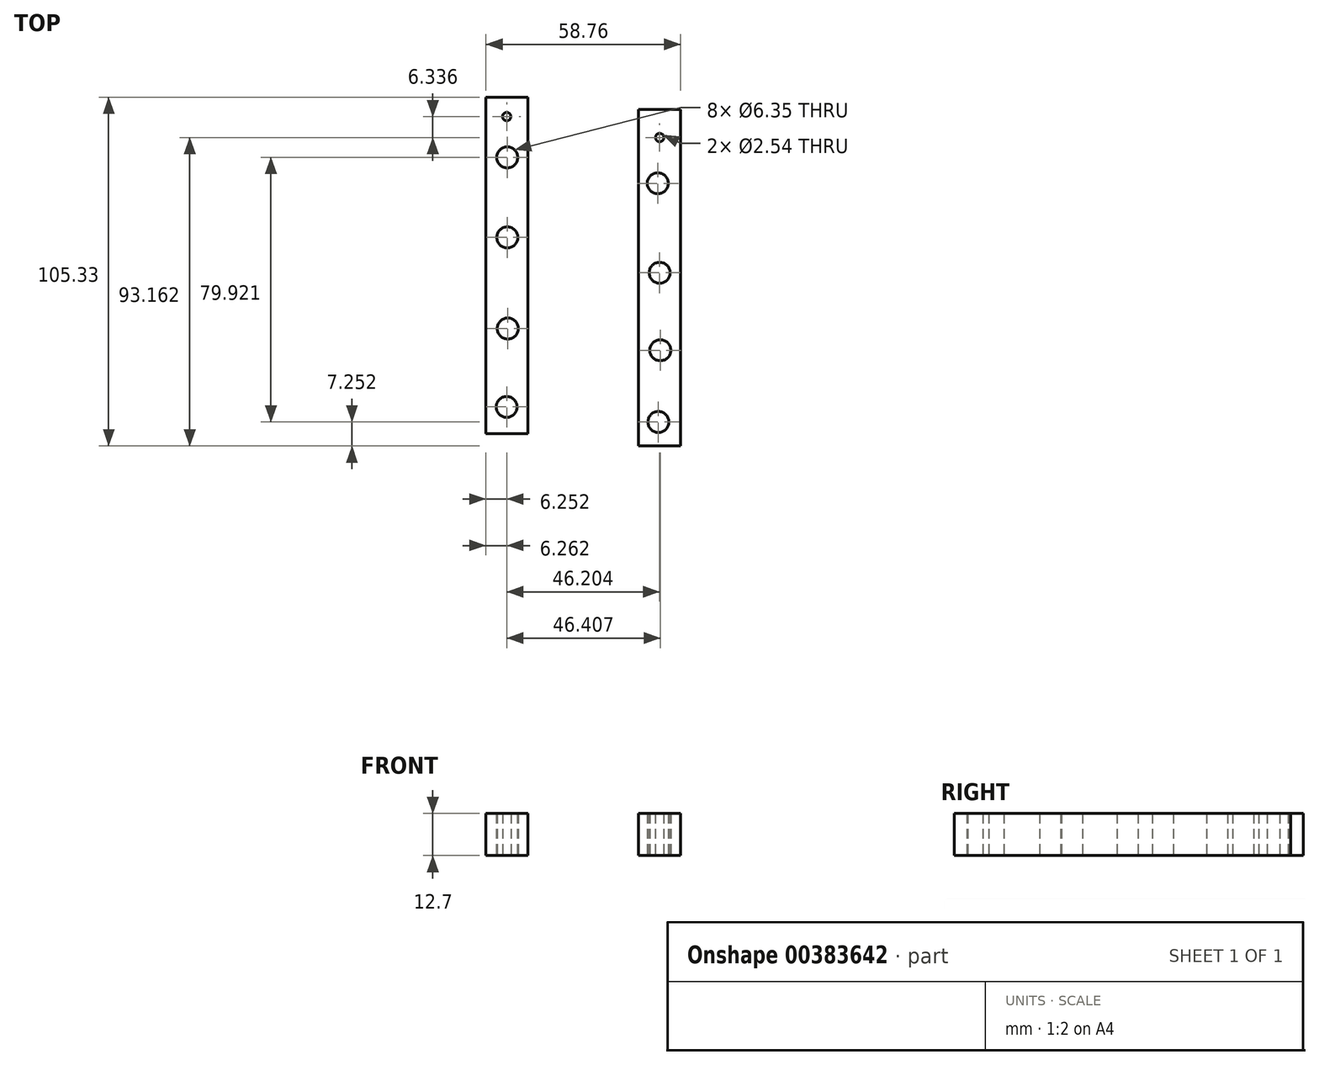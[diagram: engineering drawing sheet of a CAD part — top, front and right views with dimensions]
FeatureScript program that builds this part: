
annotation { "Feature Type Name" : "Feature", "Feature Type Description" : "" }
export const myFeature = defineFeature(function(context is Context, id is Id, definition is map)
    precondition{}
    {
        {
            var Q0;
            Q0=qCreatedBy(makeId("Top.planeOp"),FACE);
            var sketch = newSketch(context, id + "F0", { "sketchPlane" : qUnion([Q0])});
            skLineSegment(sketch, "E0.bottom", {"start": v(-28.48, -14.56) * mm, "end": v(-15.78, -14.56) * mm});
            skLineSegment(sketch, "E0.top", {"start": v(-28.48, 87.04) * mm, "end": v(-15.78, 87.04) * mm});
            skLineSegment(sketch, "E0.left", {"start": v(-28.48, -14.56) * mm, "end": v(-28.48, 87.04) * mm});
            skLineSegment(sketch, "E0.right", {"start": v(-15.78, -14.56) * mm, "end": v(-15.78, 87.04) * mm});
            skLineSegment(sketch, "E1.bottom", {"start": v(17.58, -18.3) * mm, "end": v(30.28, -18.3) * mm});
            skLineSegment(sketch, "E1.top", {"start": v(17.58, 83.3) * mm, "end": v(30.28, 83.3) * mm});
            skLineSegment(sketch, "E1.left", {"start": v(17.58, -18.3) * mm, "end": v(17.58, 83.3) * mm});
            skLineSegment(sketch, "E1.right", {"start": v(30.28, -18.3) * mm, "end": v(30.28, 83.3) * mm});
            skCircle(sketch, "E2", {"center": v(-22.23, -6.5) * mm, "radius": 3.18 * mm});
            skCircle(sketch, "E3", {"center": v(-21.87, 17.2) * mm, "radius": 3.18 * mm});
            skCircle(sketch, "E4", {"center": v(-22.03, 44.7) * mm, "radius": 3.18 * mm});
            skCircle(sketch, "E5", {"center": v(-22.22, 81.2) * mm, "radius": 1.27 * mm});
            skCircle(sketch, "E6", {"center": v(-22.04, 68.88) * mm, "radius": 3.18 * mm});
            skCircle(sketch, "E7", {"center": v(23.6, -11.04) * mm, "radius": 3.18 * mm});
            skCircle(sketch, "E8", {"center": v(24.18, 10.63) * mm, "radius": 3.18 * mm});
            skCircle(sketch, "E9", {"center": v(23.99, 34.03) * mm, "radius": 3.18 * mm});
            skCircle(sketch, "E10", {"center": v(23.41, 61.06) * mm, "radius": 3.18 * mm});
            skCircle(sketch, "E11", {"center": v(23.99, 74.87) * mm, "radius": 1.27 * mm});
            skCircle(sketch, "E12", {"center": v(-67.1, 62.22) * mm, "radius": 1.27 * mm});
            skLineSegment(sketch, "E13.top", {"start": v(-134.94, 52.5) * mm, "end": v(-33.34, 52.5) * mm});
            skLineSegment(sketch, "E13.right", {"start": v(-33.34, 27.1) * mm, "end": v(-33.34, 52.5) * mm});
            skLineSegment(sketch, "E14", {"start": v(-134.94, 39.8) * mm, "end": v(-90.4, 39.8) * mm});
            skLineSegment(sketch, "E15", {"start": v(-90.4, 39.8) * mm, "end": v(-90.4, 27.1) * mm});
            skLineSegment(sketch, "E16", {"start": v(-84.14, 39.8) * mm, "end": v(-84.14, 27.1) * mm});
            skPoint(sketch, "E16.startSnap0", {"position": v(-84.14, 27.1) * mm});
            skLineSegment(sketch, "E17", {"start": v(-87.45, 27.1) * mm, "end": v(-87.45, 39.8) * mm});
            skLineSegment(sketch, "E18", {"start": v(-81.33, 27.1) * mm, "end": v(-81.33, 39.8) * mm});
            skLineSegment(sketch, "E19", {"start": v(-78.38, 27.1) * mm, "end": v(-78.38, 39.8) * mm});
            skLineSegment(sketch, "E20", {"start": v(-75.64, 27.1) * mm, "end": v(-75.64, 39.8) * mm});
            skLineSegment(sketch, "E21", {"start": v(-72.68, 27.1) * mm, "end": v(-72.68, 39.8) * mm});
            skLineSegment(sketch, "E22", {"start": v(-69.94, 27.1) * mm, "end": v(-69.94, 39.8) * mm});
            skLineSegment(sketch, "E23", {"start": v(-67.2, 27.1) * mm, "end": v(-67.2, 39.8) * mm});
            skLineSegment(sketch, "E24", {"start": v(-63.82, 27.1) * mm, "end": v(-63.82, 39.8) * mm});
            skLineSegment(sketch, "E25", {"start": v(-61.7, 27.1) * mm, "end": v(-61.7, 39.8) * mm});
            skLineSegment(sketch, "E26", {"start": v(-58.96, 27.1) * mm, "end": v(-58.96, 39.8) * mm});
            skLineSegment(sketch, "E27", {"start": v(-56, 27.1) * mm, "end": v(-56, 39.8) * mm});
            skLineSegment(sketch, "E28", {"start": v(-50.73, 27.1) * mm, "end": v(-50.73, 39.8) * mm});
            skLineSegment(sketch, "E29", {"start": v(-48, 27.1) * mm, "end": v(-48, 39.8) * mm});
            skLineSegment(sketch, "E30", {"start": v(-45.04, 27.1) * mm, "end": v(-45.04, 39.8) * mm});
            skLineSegment(sketch, "E31", {"start": v(-38.28, 27.1) * mm, "end": v(-38.28, 39.8) * mm});
            skLineSegment(sketch, "E32", {"start": v(-35.75, 27.1) * mm, "end": v(-35.75, 39.8) * mm});
            skLineSegment(sketch, "E33", {"start": v(-53.69, 27.1) * mm, "end": v(-53.69, 39.8) * mm});
            skLineSegment(sketch, "E34", {"start": v(-41.87, 27.1) * mm, "end": v(-41.87, 39.8) * mm});
            skLineSegment(sketch, "E35", {"start": v(-90.4, 39.8) * mm, "end": v(-87.45, 39.8) * mm});
            skLineSegment(sketch, "E36", {"start": v(-84.14, 39.8) * mm, "end": v(-81.33, 39.8) * mm});
            skLineSegment(sketch, "E37", {"start": v(-78.38, 39.8) * mm, "end": v(-75.64, 39.8) * mm});
            skLineSegment(sketch, "E38", {"start": v(-72.68, 39.8) * mm, "end": v(-69.94, 39.8) * mm});
            skLineSegment(sketch, "E39", {"start": v(-67.2, 39.8) * mm, "end": v(-63.82, 39.8) * mm});
            skLineSegment(sketch, "E40", {"start": v(-61.7, 39.8) * mm, "end": v(-58.96, 39.8) * mm});
            skLineSegment(sketch, "E41", {"start": v(-56, 39.8) * mm, "end": v(-53.69, 39.8) * mm});
            skLineSegment(sketch, "E42", {"start": v(-50.73, 39.8) * mm, "end": v(-48, 39.8) * mm});
            skLineSegment(sketch, "E43", {"start": v(-45.04, 39.8) * mm, "end": v(-41.87, 39.8) * mm});
            skLineSegment(sketch, "E44", {"start": v(-38.28, 39.8) * mm, "end": v(-35.75, 39.8) * mm});
            skLineSegment(sketch, "E45", {"start": v(-90.4, 27.1) * mm, "end": v(-87.45, 27.1) * mm});
            skLineSegment(sketch, "E46", {"start": v(-84.14, 27.1) * mm, "end": v(-81.33, 27.1) * mm});
            skLineSegment(sketch, "E47", {"start": v(-78.38, 27.1) * mm, "end": v(-75.64, 27.1) * mm});
            skLineSegment(sketch, "E48", {"start": v(-72.68, 27.1) * mm, "end": v(-69.94, 27.1) * mm});
            skLineSegment(sketch, "E49", {"start": v(-67.2, 27.1) * mm, "end": v(-63.82, 27.1) * mm});
            skLineSegment(sketch, "E50", {"start": v(-61.7, 27.1) * mm, "end": v(-58.96, 27.1) * mm});
            skLineSegment(sketch, "E51", {"start": v(-56, 27.1) * mm, "end": v(-53.69, 27.1) * mm});
            skLineSegment(sketch, "E52", {"start": v(-50.73, 27.1) * mm, "end": v(-48, 27.1) * mm});
            skLineSegment(sketch, "E53", {"start": v(-45.04, 27.1) * mm, "end": v(-41.87, 27.1) * mm});
            skLineSegment(sketch, "E54", {"start": v(-38.5, 27.1) * mm, "end": v(-35.75, 27.1) * mm});
            skLineSegment(sketch, "E55", {"start": v(-33.34, 27.1) * mm, "end": v(-35.75, 27.1) * mm});
            skLineSegment(sketch, "E56", {"start": v(-134.94, 52.5) * mm, "end": v(-134.94, 39.8) * mm});
            skSolve(sketch);
        }
        {
            var Q0;
            Q0=makeQuery(id+"F0.imprint","IMPRINT",FACE,{"disambiguationData":[TD([[makeQuery(id+"F0.imprint","IMPRINT",EDGE,{"derivedFrom":sQuery(id+"F0.wireOp",EDGE,"E0.bottom")}),1.0]])]});
            extrude(context, id + "F1", {"entities" : qUnion([Q0]), "depth" : 12.7 * mm});
        }
        {
            var Q0;
            Q0=makeQuery(id+"F0.imprint","IMPRINT",FACE,{"disambiguationData":[TD([[makeQuery(id+"F0.imprint","IMPRINT",EDGE,{"derivedFrom":sQuery(id+"F0.wireOp",EDGE,"E1.bottom")}),1.0]])]});
            extrude(context, id + "F2", {"entities" : qUnion([Q0]), "depth" : 12.7 * mm});
        }
    });
